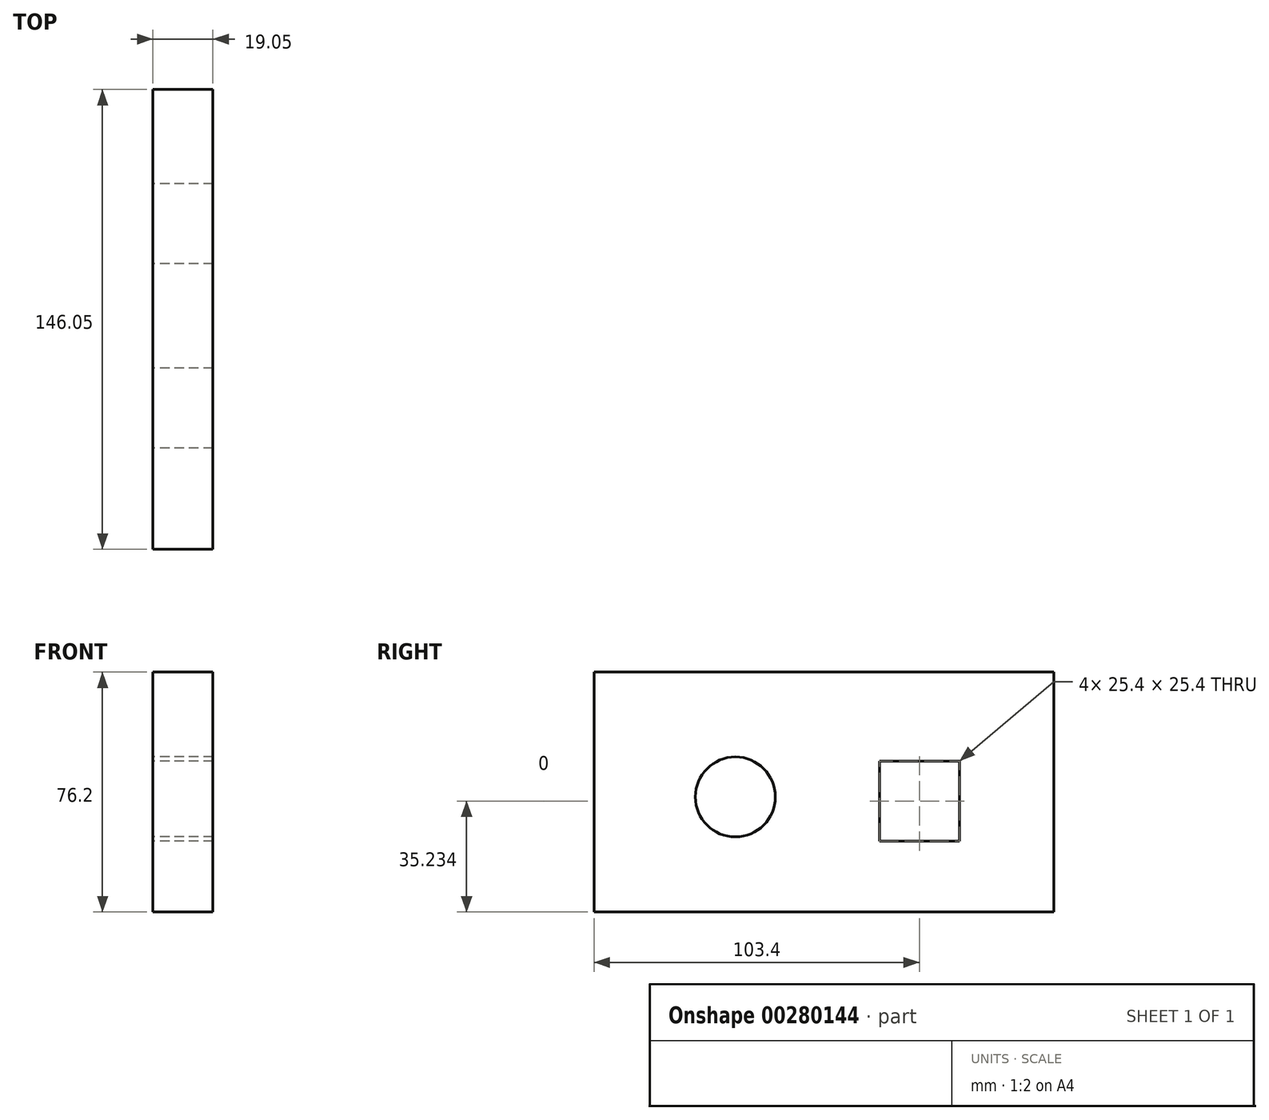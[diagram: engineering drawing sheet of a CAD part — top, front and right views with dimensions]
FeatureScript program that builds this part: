
annotation { "Feature Type Name" : "Feature", "Feature Type Description" : "" }
export const myFeature = defineFeature(function(context is Context, id is Id, definition is map)
    precondition{}
    {
        {
            var Q0;
            Q0=qCreatedBy(makeId("Right.planeOp"),FACE);
            var sketch = newSketch(context, id + "F0", { "sketchPlane" : qUnion([Q0])});
            skLineSegment(sketch, "E0.bottom", {"start": v(85.33, 48.51) * mm, "end": v(-60.72, 48.51) * mm});
            skLineSegment(sketch, "E0.top", {"start": v(85.33, -27.69) * mm, "end": v(-60.72, -27.69) * mm});
            skLineSegment(sketch, "E0.left", {"start": v(85.33, 48.51) * mm, "end": v(85.33, -27.69) * mm});
            skLineSegment(sketch, "E0.right", {"start": v(-60.72, 48.51) * mm, "end": v(-60.72, -27.69) * mm});
            skCircle(sketch, "E1", {"center": v(-15.8, 8.87) * mm, "radius": 12.7 * mm});
            skLineSegment(sketch, "E2.bottom", {"start": v(55.38, 20.24) * mm, "end": v(29.98, 20.24) * mm});
            skLineSegment(sketch, "E2.top", {"start": v(55.38, -5.16) * mm, "end": v(29.98, -5.16) * mm});
            skLineSegment(sketch, "E2.left", {"start": v(55.38, 20.24) * mm, "end": v(55.38, -5.16) * mm});
            skLineSegment(sketch, "E2.right", {"start": v(29.98, 20.24) * mm, "end": v(29.98, -5.16) * mm});
            skSolve(sketch);
        }
        {
            var Q0;
            Q0=makeQuery(id+"F0.imprint","IMPRINT",FACE,{"disambiguationData":[TD([[makeQuery(id+"F0.imprint","IMPRINT",EDGE,{"derivedFrom":sQuery(id+"F0.wireOp",EDGE,"E0.bottom")}),1.0]])]});
            extrude(context, id + "F1", {"entities" : qUnion([Q0]), "depth" : 19.05 * mm});
        }
    });
